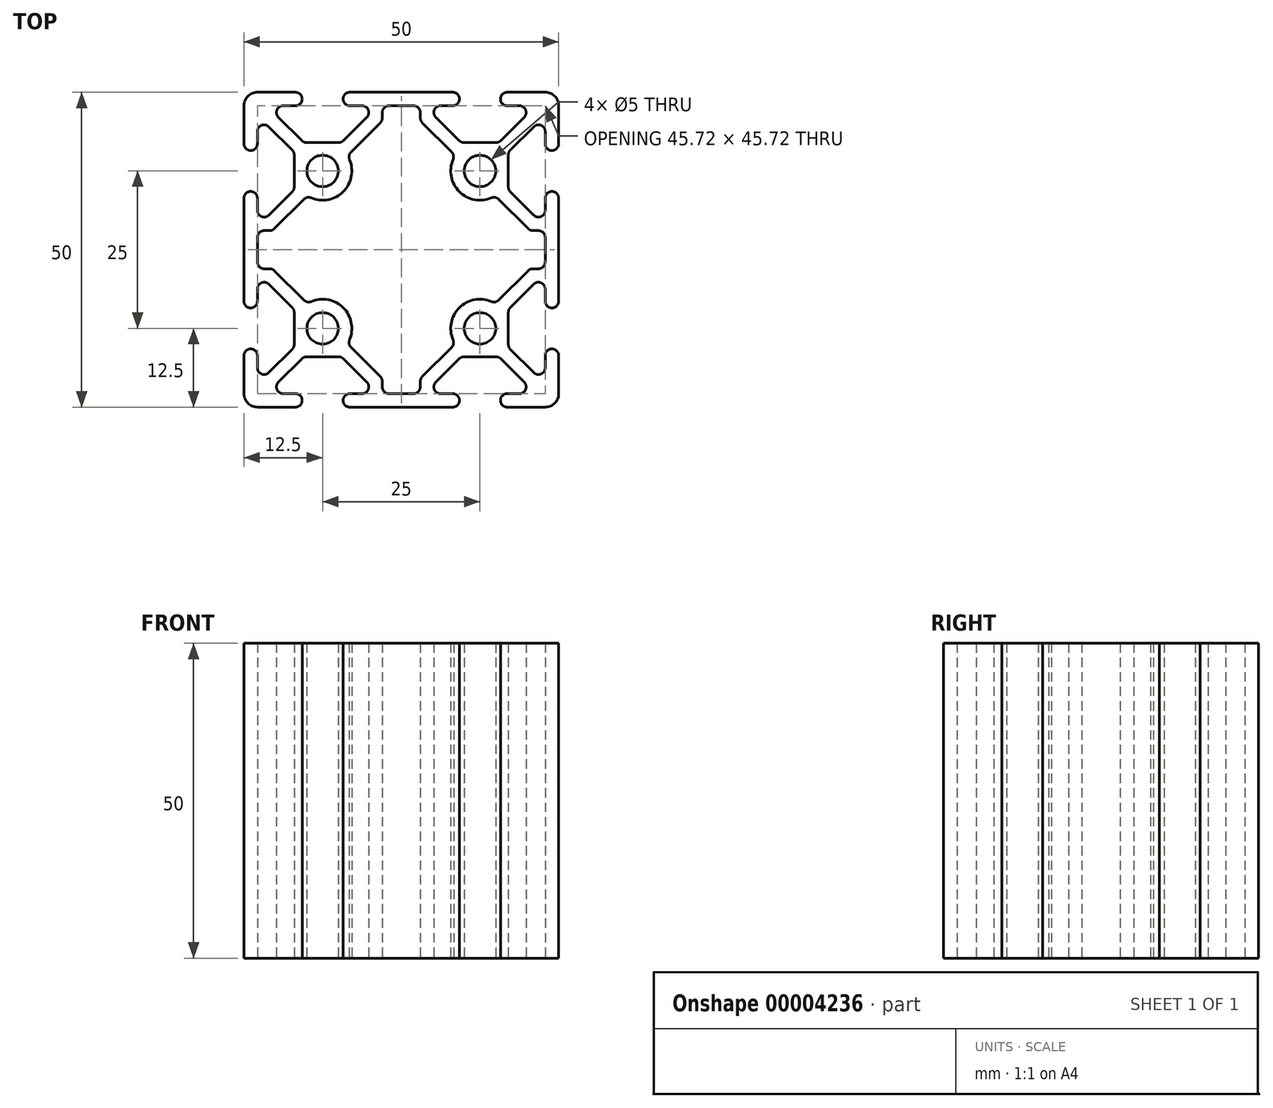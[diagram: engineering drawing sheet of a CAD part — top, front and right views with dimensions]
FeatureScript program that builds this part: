
annotation { "Feature Type Name" : "Feature", "Feature Type Description" : "" }
export const myFeature = defineFeature(function(context is Context, id is Id, definition is map)
    precondition{}
    {
        {
            var Q0;
            Q0=qCreatedBy(makeId("Top.planeOp"),FACE);
            var sketch = newSketch(context, id + "F0", { "sketchPlane" : qUnion([Q0])});
            skLineSegment(sketch, "E0", {"start": v(-12.5, 12.5) * mm, "end": v(-25, 25) * mm, "construction": true});
            skLineSegment(sketch, "E1", {"start": v(-25, 22.86) * mm, "end": v(-25, 16.82) * mm});
            skLineSegment(sketch, "E2", {"start": v(-22.86, 25) * mm, "end": v(-16.82, 25) * mm});
            skLineSegment(sketch, "E3", {"start": v(-16.82, 22.86) * mm, "end": v(-18.76, 22.86) * mm});
            skLineSegment(sketch, "E4", {"start": v(-22.86, 18.76) * mm, "end": v(-22.86, 16.82) * mm});
            skArc(sketch, "E5", {"start": v(-16.82, 25) * mm, "mid": v(-15.75, 23.93) * mm, "end": v(-16.82, 22.86) * mm});
            skArc(sketch, "E6", {"start": v(-22.86, 16.82) * mm, "mid": v(-23.93, 15.75) * mm, "end": v(-25, 16.82) * mm});
            skLineSegment(sketch, "E7", {"start": v(-19.52, 21.03) * mm, "end": v(-15.81, 17.32) * mm});
            skPoint(sketch, "E8.visualSharp", {"position": v(-25, 25) * mm});
            skLineSegment(sketch, "E8.filletArc", {"start": v(-25, 25) * mm, "end": v(-25, 25) * mm});
            skArc(sketch, "E9.filletArc", {"start": v(-21.03, 19.52) * mm, "mid": v(-22.2, 19.75) * mm, "end": v(-22.86, 18.76) * mm});
            skPoint(sketch, "E10.visualSharp", {"position": v(-21.35, 22.86) * mm});
            skArc(sketch, "E10.filletArc", {"start": v(-18.76, 22.86) * mm, "mid": v(-19.75, 22.2) * mm, "end": v(-19.52, 21.03) * mm});
            skArc(sketch, "E11.filletArc", {"start": v(-15.81, 17.32) * mm, "mid": v(-15.46, 17.1) * mm, "end": v(-15.05, 17.01) * mm});
            skCircle(sketch, "E12", {"center": v(-12.5, 12.5) * mm, "radius": 2.5 * mm});
            skLineSegment(sketch, "E13", {"start": v(0, 0) * mm, "end": v(0, 12.39) * mm, "construction": true});
            skCircle(sketch, "E14.0.MirrorC", {"center": v(12.5, 12.5) * mm, "radius": 2.5 * mm});
            skLineSegment(sketch, "E15", {"start": v(-12.5, 0) * mm, "end": v(-12.5, 12.5) * mm, "construction": true});
            skArc(sketch, "E16.0.MirrorCS", {"start": v(-9.19, 17.32) * mm, "mid": v(-9.54, 17.1) * mm, "end": v(-9.95, 17.01) * mm});
            skLineSegment(sketch, "E16.1.MirrorCS", {"start": v(-8.18, 22.86) * mm, "end": v(-6.24, 22.86) * mm});
            skLineSegment(sketch, "E16.3.MirrorCS", {"start": v(-5.48, 21.03) * mm, "end": v(-9.19, 17.32) * mm});
            skArc(sketch, "E16.8.MirrorCS", {"start": v(-8.18, 25) * mm, "mid": v(-9.25, 23.93) * mm, "end": v(-8.18, 22.86) * mm});
            skArc(sketch, "E16.11.MirrorCS", {"start": v(-6.24, 22.86) * mm, "mid": v(-5.25, 22.2) * mm, "end": v(-5.48, 21.03) * mm});
            skLineSegment(sketch, "E16.17.MirrorCS", {"start": v(0, 25) * mm, "end": v(-8.18, 25) * mm});
            skLineSegment(sketch, "E17", {"start": v(-15.05, 17.01) * mm, "end": v(-9.95, 17.01) * mm});
            skArc(sketch, "E18.1.MirrorCS", {"start": v(15.81, 17.32) * mm, "mid": v(15.46, 17.1) * mm, "end": v(15.05, 17.01) * mm});
            skArc(sketch, "E18.2.MirrorCS", {"start": v(9.19, 17.32) * mm, "mid": v(9.54, 17.1) * mm, "end": v(9.95, 17.01) * mm});
            skArc(sketch, "E18.3.MirrorCS", {"start": v(22.86, 16.82) * mm, "mid": v(23.93, 15.75) * mm, "end": v(25, 16.82) * mm});
            skLineSegment(sketch, "E18.5.MirrorCS", {"start": v(8.18, 22.86) * mm, "end": v(6.24, 22.86) * mm});
            skLineSegment(sketch, "E18.6.MirrorCS", {"start": v(19.52, 21.03) * mm, "end": v(15.81, 17.32) * mm});
            skLineSegment(sketch, "E18.7.MirrorCS", {"start": v(5.48, 21.03) * mm, "end": v(9.19, 17.32) * mm});
            skLineSegment(sketch, "E18.8.MirrorCS", {"start": v(12.5, 12.5) * mm, "end": v(25, 25) * mm, "construction": true});
            skArc(sketch, "E18.10.MirrorCS", {"start": v(16.82, 25) * mm, "mid": v(15.75, 23.93) * mm, "end": v(16.82, 22.86) * mm});
            skLineSegment(sketch, "E18.11.MirrorCS", {"start": v(15.05, 17.01) * mm, "end": v(9.95, 17.01) * mm});
            skPoint(sketch, "E18.12.MirrorP", {"position": v(21.35, 22.86) * mm});
            skLineSegment(sketch, "E18.14.MirrorCS", {"start": v(22.86, 25) * mm, "end": v(16.82, 25) * mm});
            skArc(sketch, "E18.15.MirrorCS", {"start": v(21.03, 19.52) * mm, "mid": v(22.2, 19.75) * mm, "end": v(22.86, 18.76) * mm});
            skPoint(sketch, "E18.16.MirrorP", {"position": v(25, 25) * mm});
            skLineSegment(sketch, "E18.17.MirrorCS", {"start": v(25, 22.86) * mm, "end": v(25, 16.82) * mm});
            skArc(sketch, "E18.18.MirrorCS", {"start": v(6.24, 22.86) * mm, "mid": v(5.25, 22.2) * mm, "end": v(5.48, 21.03) * mm});
            skArc(sketch, "E18.20.MirrorCS", {"start": v(18.76, 22.86) * mm, "mid": v(19.75, 22.2) * mm, "end": v(19.52, 21.03) * mm});
            skArc(sketch, "E18.21.MirrorCS", {"start": v(8.18, 25) * mm, "mid": v(9.25, 23.93) * mm, "end": v(8.18, 22.86) * mm});
            skLineSegment(sketch, "E18.22.MirrorCS", {"start": v(25, 25) * mm, "end": v(25, 25) * mm});
            skLineSegment(sketch, "E18.24.MirrorCS", {"start": v(22.86, 18.76) * mm, "end": v(22.86, 16.82) * mm});
            skLineSegment(sketch, "E18.25.MirrorCS", {"start": v(16.82, 22.86) * mm, "end": v(18.76, 22.86) * mm});
            skLineSegment(sketch, "E18.26.MirrorCS", {"start": v(0, 25) * mm, "end": v(8.18, 25) * mm});
            skLineSegment(sketch, "E19", {"start": v(-21.03, 19.52) * mm, "end": v(-17.32, 15.81) * mm});
            skLineSegment(sketch, "E20", {"start": v(0, 0) * mm, "end": v(-29.45, 0) * mm, "construction": true});
            skLineSegment(sketch, "E21", {"start": v(-17, 15.05) * mm, "end": v(-17, 12.5) * mm});
            skLineSegment(sketch, "E22", {"start": v(-12.5, 12.5) * mm, "end": v(-25, 12.5) * mm, "construction": true});
            skLineSegment(sketch, "E23.0.MirrorCS", {"start": v(21.03, 19.52) * mm, "end": v(17.32, 15.81) * mm});
            skLineSegment(sketch, "E24.0.MirrorCS", {"start": v(17, 15.05) * mm, "end": v(17, 12.5) * mm});
            skLineSegment(sketch, "E25.0.MirrorCS", {"start": v(-17, 9.95) * mm, "end": v(-17, 12.5) * mm});
            skLineSegment(sketch, "E26.0.MirrorCS", {"start": v(-21.03, 5.48) * mm, "end": v(-17.32, 9.19) * mm});
            skArc(sketch, "E27.0.MirrorCS", {"start": v(-21.03, 5.48) * mm, "mid": v(-22.2, 5.25) * mm, "end": v(-22.86, 6.24) * mm});
            skLineSegment(sketch, "E28.0.MirrorCS", {"start": v(-22.86, 6.24) * mm, "end": v(-22.86, 8.18) * mm});
            skArc(sketch, "E29.0.MirrorCS", {"start": v(-22.86, 8.18) * mm, "mid": v(-23.93, 9.25) * mm, "end": v(-25, 8.18) * mm});
            skLineSegment(sketch, "E30.0.MirrorCS", {"start": v(-25, 0) * mm, "end": v(-25, 8.18) * mm});
            skLineSegment(sketch, "E31.0.MirrorCS", {"start": v(17, 9.95) * mm, "end": v(17, 12.5) * mm});
            skLineSegment(sketch, "E32.0.MirrorCS", {"start": v(21.03, 5.48) * mm, "end": v(17.32, 9.19) * mm});
            skArc(sketch, "E33.0.MirrorCS", {"start": v(21.03, 5.48) * mm, "mid": v(22.2, 5.25) * mm, "end": v(22.86, 6.24) * mm});
            skLineSegment(sketch, "E34.0.MirrorCS", {"start": v(22.86, 6.24) * mm, "end": v(22.86, 8.18) * mm});
            skArc(sketch, "E35.0.MirrorCS", {"start": v(22.86, 8.18) * mm, "mid": v(23.93, 9.25) * mm, "end": v(25, 8.18) * mm});
            skLineSegment(sketch, "E36.0.MirrorCS", {"start": v(25, 0) * mm, "end": v(25, 8.18) * mm});
            skPoint(sketch, "E37.visualSharp", {"position": v(-17, 15.5) * mm});
            skArc(sketch, "E37.filletArc", {"start": v(-17, 15.05) * mm, "mid": v(-17.1, 15.46) * mm, "end": v(-17.32, 15.81) * mm});
            skPoint(sketch, "E38.visualSharp", {"position": v(-17, 9.5) * mm});
            skArc(sketch, "E38.filletArc", {"start": v(-17.32, 9.19) * mm, "mid": v(-17.1, 9.54) * mm, "end": v(-17, 9.95) * mm});
            skPoint(sketch, "E39.visualSharp", {"position": v(17, 9.5) * mm});
            skArc(sketch, "E39.filletArc", {"start": v(17, 9.95) * mm, "mid": v(17.1, 9.54) * mm, "end": v(17.32, 9.19) * mm});
            skPoint(sketch, "E40.visualSharp", {"position": v(17, 15.5) * mm});
            skArc(sketch, "E40.filletArc", {"start": v(17.32, 15.81) * mm, "mid": v(17.1, 15.46) * mm, "end": v(17, 15.05) * mm});
            skArc(sketch, "E41.0.MirrorCS", {"start": v(-17, -15.05) * mm, "mid": v(-17.1, -15.46) * mm, "end": v(-17.32, -15.81) * mm});
            skArc(sketch, "E41.1.MirrorCS", {"start": v(-17.32, -9.19) * mm, "mid": v(-17.1, -9.54) * mm, "end": v(-17, -9.95) * mm});
            skArc(sketch, "E41.2.MirrorCS", {"start": v(-9.19, -17.32) * mm, "mid": v(-9.54, -17.1) * mm, "end": v(-9.95, -17.01) * mm});
            skArc(sketch, "E41.3.MirrorCS", {"start": v(-15.81, -17.32) * mm, "mid": v(-15.46, -17.1) * mm, "end": v(-15.05, -17.01) * mm});
            skLineSegment(sketch, "E41.4.MirrorCS", {"start": v(-25, -25) * mm, "end": v(-25, -25) * mm});
            skLineSegment(sketch, "E41.5.MirrorCS", {"start": v(-22.86, -6.24) * mm, "end": v(-22.86, -8.18) * mm});
            skLineSegment(sketch, "E41.6.MirrorCS", {"start": v(-12.5, -12.5) * mm, "end": v(-25, -25) * mm, "construction": true});
            skLineSegment(sketch, "E41.7.MirrorCS", {"start": v(-8.18, -22.86) * mm, "end": v(-6.24, -22.86) * mm});
            skLineSegment(sketch, "E41.8.MirrorCS", {"start": v(-12.5, 0) * mm, "end": v(-12.5, -12.5) * mm, "construction": true});
            skLineSegment(sketch, "E41.9.MirrorCS", {"start": v(-5.48, -21.03) * mm, "end": v(-9.19, -17.32) * mm});
            skCircle(sketch, "E41.10.MirrorC", {"center": v(-12.5, -12.5) * mm, "radius": 2.5 * mm});
            skArc(sketch, "E41.11.MirrorCS", {"start": v(-18.76, -22.86) * mm, "mid": v(-19.75, -22.2) * mm, "end": v(-19.52, -21.03) * mm});
            skArc(sketch, "E41.12.MirrorCS", {"start": v(-21.03, -5.48) * mm, "mid": v(-22.2, -5.25) * mm, "end": v(-22.86, -6.24) * mm});
            skLineSegment(sketch, "E41.13.MirrorCS", {"start": v(-15.05, -17.01) * mm, "end": v(-9.95, -17.01) * mm});
            skPoint(sketch, "E41.14.MirrorP", {"position": v(-17, -9.5) * mm});
            skLineSegment(sketch, "E41.15.MirrorCS", {"start": v(-21.03, -5.48) * mm, "end": v(-17.32, -9.19) * mm});
            skLineSegment(sketch, "E41.16.MirrorCS", {"start": v(-19.52, -21.03) * mm, "end": v(-15.81, -17.32) * mm});
            skArc(sketch, "E41.17.MirrorCS", {"start": v(-6.24, -22.86) * mm, "mid": v(-5.25, -22.2) * mm, "end": v(-5.48, -21.03) * mm});
            skLineSegment(sketch, "E41.18.MirrorCS", {"start": v(-25, 0) * mm, "end": v(-25, -8.18) * mm});
            skArc(sketch, "E41.19.MirrorCS", {"start": v(-21.03, -19.52) * mm, "mid": v(-22.2, -19.75) * mm, "end": v(-22.86, -18.76) * mm});
            skArc(sketch, "E41.20.MirrorCS", {"start": v(-16.82, -25) * mm, "mid": v(-15.75, -23.93) * mm, "end": v(-16.82, -22.86) * mm});
            skArc(sketch, "E41.21.MirrorCS", {"start": v(-22.86, -16.82) * mm, "mid": v(-23.93, -15.75) * mm, "end": v(-25, -16.82) * mm});
            skLineSegment(sketch, "E41.22.MirrorCS", {"start": v(-17, -15.05) * mm, "end": v(-17, -12.5) * mm});
            skPoint(sketch, "E41.23.MirrorP", {"position": v(-17, -15.5) * mm});
            skArc(sketch, "E41.24.MirrorCS", {"start": v(-22.86, -8.18) * mm, "mid": v(-23.93, -9.25) * mm, "end": v(-25, -8.18) * mm});
            skLineSegment(sketch, "E41.25.MirrorCS", {"start": v(-21.03, -19.52) * mm, "end": v(-17.32, -15.81) * mm});
            skPoint(sketch, "E41.26.MirrorP", {"position": v(-21.35, -22.86) * mm});
            skArc(sketch, "E41.27.MirrorCS", {"start": v(-8.18, -25) * mm, "mid": v(-9.25, -23.93) * mm, "end": v(-8.18, -22.86) * mm});
            skPoint(sketch, "E41.28.MirrorP", {"position": v(-25, -25) * mm});
            skLineSegment(sketch, "E41.29.MirrorCS", {"start": v(-12.5, -12.5) * mm, "end": v(-25, -12.5) * mm, "construction": true});
            skLineSegment(sketch, "E41.30.MirrorCS", {"start": v(-17, -9.95) * mm, "end": v(-17, -12.5) * mm});
            skLineSegment(sketch, "E41.31.MirrorCS", {"start": v(-16.82, -22.86) * mm, "end": v(-18.76, -22.86) * mm});
            skLineSegment(sketch, "E41.32.MirrorCS", {"start": v(-22.86, -18.76) * mm, "end": v(-22.86, -16.82) * mm});
            skLineSegment(sketch, "E41.33.MirrorCS", {"start": v(-25, -22.86) * mm, "end": v(-25, -16.82) * mm});
            skLineSegment(sketch, "E41.34.MirrorCS", {"start": v(-22.86, -25) * mm, "end": v(-16.82, -25) * mm});
            skLineSegment(sketch, "E41.35.MirrorCS", {"start": v(0, -25) * mm, "end": v(-8.18, -25) * mm});
            skArc(sketch, "E42.0.MirrorCS", {"start": v(17.32, -15.81) * mm, "mid": v(17.1, -15.46) * mm, "end": v(17, -15.05) * mm});
            skArc(sketch, "E42.1.MirrorCS", {"start": v(17, -9.95) * mm, "mid": v(17.1, -9.54) * mm, "end": v(17.32, -9.19) * mm});
            skArc(sketch, "E42.2.MirrorCS", {"start": v(9.19, -17.32) * mm, "mid": v(9.54, -17.1) * mm, "end": v(9.95, -17.01) * mm});
            skLineSegment(sketch, "E42.3.MirrorCS", {"start": v(22.86, -6.24) * mm, "end": v(22.86, -8.18) * mm});
            skLineSegment(sketch, "E42.4.MirrorCS", {"start": v(16.82, -22.86) * mm, "end": v(18.76, -22.86) * mm});
            skArc(sketch, "E42.5.MirrorCS", {"start": v(15.81, -17.32) * mm, "mid": v(15.46, -17.1) * mm, "end": v(15.05, -17.01) * mm});
            skLineSegment(sketch, "E42.6.MirrorCS", {"start": v(25, -25) * mm, "end": v(25, -25) * mm});
            skArc(sketch, "E42.7.MirrorCS", {"start": v(22.86, -16.82) * mm, "mid": v(23.93, -15.75) * mm, "end": v(25, -16.82) * mm});
            skArc(sketch, "E42.8.MirrorCS", {"start": v(16.82, -25) * mm, "mid": v(15.75, -23.93) * mm, "end": v(16.82, -22.86) * mm});
            skPoint(sketch, "E42.9.MirrorP", {"position": v(25, -25) * mm});
            skArc(sketch, "E42.10.MirrorCS", {"start": v(21.03, -5.48) * mm, "mid": v(22.2, -5.25) * mm, "end": v(22.86, -6.24) * mm});
            skLineSegment(sketch, "E42.11.MirrorCS", {"start": v(0, -25) * mm, "end": v(8.18, -25) * mm});
            skArc(sketch, "E42.12.MirrorCS", {"start": v(8.18, -25) * mm, "mid": v(9.25, -23.93) * mm, "end": v(8.18, -22.86) * mm});
            skLineSegment(sketch, "E42.13.MirrorCS", {"start": v(22.86, -25) * mm, "end": v(16.82, -25) * mm});
            skPoint(sketch, "E42.14.MirrorP", {"position": v(17, -15.5) * mm});
            skArc(sketch, "E42.15.MirrorCS", {"start": v(21.03, -19.52) * mm, "mid": v(22.2, -19.75) * mm, "end": v(22.86, -18.76) * mm});
            skLineSegment(sketch, "E42.16.MirrorCS", {"start": v(17, -9.95) * mm, "end": v(17, -12.5) * mm});
            skLineSegment(sketch, "E42.17.MirrorCS", {"start": v(22.86, -18.76) * mm, "end": v(22.86, -16.82) * mm});
            skArc(sketch, "E42.18.MirrorCS", {"start": v(6.24, -22.86) * mm, "mid": v(5.25, -22.2) * mm, "end": v(5.48, -21.03) * mm});
            skLineSegment(sketch, "E42.19.MirrorCS", {"start": v(5.48, -21.03) * mm, "end": v(9.19, -17.32) * mm});
            skLineSegment(sketch, "E42.20.MirrorCS", {"start": v(15.05, -17.01) * mm, "end": v(9.95, -17.01) * mm});
            skLineSegment(sketch, "E42.21.MirrorCS", {"start": v(17, -15.05) * mm, "end": v(17, -12.5) * mm});
            skArc(sketch, "E42.22.MirrorCS", {"start": v(22.86, -8.18) * mm, "mid": v(23.93, -9.25) * mm, "end": v(25, -8.18) * mm});
            skLineSegment(sketch, "E42.23.MirrorCS", {"start": v(8.18, -22.86) * mm, "end": v(6.24, -22.86) * mm});
            skPoint(sketch, "E42.24.MirrorP", {"position": v(17, -9.5) * mm});
            skLineSegment(sketch, "E42.25.MirrorCS", {"start": v(21.03, -5.48) * mm, "end": v(17.32, -9.19) * mm});
            skLineSegment(sketch, "E42.26.MirrorCS", {"start": v(25, -22.86) * mm, "end": v(25, -16.82) * mm});
            skCircle(sketch, "E42.27.MirrorC", {"center": v(12.5, -12.5) * mm, "radius": 2.5 * mm});
            skLineSegment(sketch, "E42.28.MirrorCS", {"start": v(12.5, -12.5) * mm, "end": v(25, -25) * mm, "construction": true});
            skPoint(sketch, "E42.29.MirrorP", {"position": v(21.35, -22.86) * mm});
            skLineSegment(sketch, "E42.30.MirrorCS", {"start": v(25, 0) * mm, "end": v(25, -8.18) * mm});
            skArc(sketch, "E42.31.MirrorCS", {"start": v(22.86, -16.82) * mm, "mid": v(23.93, -15.75) * mm, "end": v(25, -16.82) * mm});
            skLineSegment(sketch, "E42.32.MirrorCS", {"start": v(19.52, -21.03) * mm, "end": v(15.81, -17.32) * mm});
            skLineSegment(sketch, "E42.33.MirrorCS", {"start": v(21.03, -19.52) * mm, "end": v(17.32, -15.81) * mm});
            skArc(sketch, "E42.34.MirrorCS", {"start": v(18.76, -22.86) * mm, "mid": v(19.75, -22.2) * mm, "end": v(19.52, -21.03) * mm});
            skArc(sketch, "E43.filletArc", {"start": v(-22.86, 25) * mm, "mid": v(-24.37, 24.37) * mm, "end": v(-25, 22.86) * mm});
            skArc(sketch, "E44.filletArc", {"start": v(25, 22.86) * mm, "mid": v(24.37, 24.37) * mm, "end": v(22.86, 25) * mm});
            skArc(sketch, "E45.filletArc", {"start": v(22.86, -25) * mm, "mid": v(24.37, -24.37) * mm, "end": v(25, -22.86) * mm});
            skArc(sketch, "E46.filletArc", {"start": v(-25, -22.86) * mm, "mid": v(-24.37, -24.37) * mm, "end": v(-22.86, -25) * mm});
            skLineSegment(sketch, "E47", {"start": v(0, 22.86) * mm, "end": v(1.96, 22.86) * mm});
            skLineSegment(sketch, "E48", {"start": v(3.03, 21.8) * mm, "end": v(3.03, 20.9) * mm});
            skArc(sketch, "E49.0", {"start": v(14.31, 8.23) * mm, "mid": v(9.22, 9.22) * mm, "end": v(8.23, 14.31) * mm});
            skLineSegment(sketch, "E50.0", {"start": v(3.34, 20.15) * mm, "end": v(8, 15.49) * mm});
            skPoint(sketch, "E51.visualSharp", {"position": v(3.03, 22.86) * mm});
            skArc(sketch, "E51.filletArc", {"start": v(3.03, 21.8) * mm, "mid": v(2.71, 22.55) * mm, "end": v(1.96, 22.86) * mm});
            skPoint(sketch, "E52.visualSharp", {"position": v(8.55, 14.94) * mm});
            skArc(sketch, "E52.filletArc", {"start": v(8.23, 14.31) * mm, "mid": v(8.3, 14.93) * mm, "end": v(8, 15.49) * mm});
            skArc(sketch, "E53.0.MirrorCS", {"start": v(-14.31, 8.23) * mm, "mid": v(-9.22, 9.22) * mm, "end": v(-8.23, 14.31) * mm});
            skArc(sketch, "E54.0.MirrorCS", {"start": v(-8.23, 14.31) * mm, "mid": v(-8.3, 14.93) * mm, "end": v(-8, 15.49) * mm});
            skArc(sketch, "E55.0.MirrorCS", {"start": v(-3.03, 21.8) * mm, "mid": v(-2.71, 22.55) * mm, "end": v(-1.96, 22.86) * mm});
            skLineSegment(sketch, "E56.0.MirrorCS", {"start": v(0, 22.86) * mm, "end": v(-1.96, 22.86) * mm});
            skPoint(sketch, "E57.visualSharp", {"position": v(3.03, 20.46) * mm});
            skArc(sketch, "E57.filletArc", {"start": v(3.03, 20.9) * mm, "mid": v(3.1, 20.5) * mm, "end": v(3.34, 20.15) * mm});
            skLineSegment(sketch, "E58.0.MirrorCS", {"start": v(-3.34, 20.15) * mm, "end": v(-8, 15.49) * mm});
            skArc(sketch, "E59.0.MirrorCS", {"start": v(-3.03, 20.9) * mm, "mid": v(-3.1, 20.5) * mm, "end": v(-3.34, 20.15) * mm});
            skLineSegment(sketch, "E60.0.MirrorCS", {"start": v(-3.03, 21.8) * mm, "end": v(-3.03, 20.9) * mm});
            skPoint(sketch, "E61.visualSharp", {"position": v(-12.5, 7.86) * mm});
            skPoint(sketch, "E62.visualSharp", {"position": v(-12.5, -7.86) * mm});
            skPoint(sketch, "E63.visualSharp", {"position": v(12.5, -7.86) * mm});
            skArc(sketch, "E64.0.MirrorCS", {"start": v(-14.31, 8.23) * mm, "mid": v(-14.93, 8.3) * mm, "end": v(-15.49, 8) * mm});
            skLineSegment(sketch, "E65.0.MirrorCS", {"start": v(-20.15, 3.34) * mm, "end": v(-15.49, 8) * mm});
            skArc(sketch, "E66.0.MirrorCS", {"start": v(-20.9, 3.03) * mm, "mid": v(-20.5, 3.1) * mm, "end": v(-20.15, 3.34) * mm});
            skLineSegment(sketch, "E67.0.MirrorCS", {"start": v(-21.79, 3.03) * mm, "end": v(-20.9, 3.03) * mm});
            skArc(sketch, "E68.0.MirrorCS", {"start": v(-21.79, 3.03) * mm, "mid": v(-22.55, 2.71) * mm, "end": v(-22.86, 1.96) * mm});
            skLineSegment(sketch, "E69.0.MirrorCS", {"start": v(-22.86, 0) * mm, "end": v(-22.86, 1.96) * mm});
            skArc(sketch, "E70.0.MirrorCS", {"start": v(14.31, 8.23) * mm, "mid": v(14.93, 8.3) * mm, "end": v(15.49, 8) * mm});
            skArc(sketch, "E71.0.MirrorCS", {"start": v(-12.5, 7.86) * mm, "mid": v(-8.63, 9.94) * mm, "end": v(-8.23, 14.31) * mm});
            skLineSegment(sketch, "E72.0.MirrorCS", {"start": v(20.15, 3.34) * mm, "end": v(15.49, 8) * mm});
            skArc(sketch, "E73.0.MirrorCS", {"start": v(20.9, 3.03) * mm, "mid": v(20.5, 3.1) * mm, "end": v(20.15, 3.34) * mm});
            skLineSegment(sketch, "E74.0.MirrorCS", {"start": v(21.79, 3.03) * mm, "end": v(20.9, 3.03) * mm});
            skArc(sketch, "E75.0.MirrorCS", {"start": v(21.79, 3.03) * mm, "mid": v(22.55, 2.71) * mm, "end": v(22.86, 1.96) * mm});
            skLineSegment(sketch, "E76.0.MirrorCS", {"start": v(22.86, 0) * mm, "end": v(22.86, 1.96) * mm});
            skPoint(sketch, "E77.orphan", {"position": v(12.5, 7.86) * mm});
            skArc(sketch, "E78.0.MirrorCS", {"start": v(-20.9, -3.03) * mm, "mid": v(-20.5, -3.1) * mm, "end": v(-20.15, -3.34) * mm});
            skLineSegment(sketch, "E78.1.MirrorCS", {"start": v(-21.79, -3.03) * mm, "end": v(-20.9, -3.03) * mm});
            skArc(sketch, "E78.2.MirrorCS", {"start": v(-21.79, -3.03) * mm, "mid": v(-22.55, -2.71) * mm, "end": v(-22.86, -1.96) * mm});
            skLineSegment(sketch, "E78.3.MirrorCS", {"start": v(-22.86, 0) * mm, "end": v(-22.86, -1.96) * mm});
            skLineSegment(sketch, "E79.0.MirrorCS", {"start": v(-20.15, -3.34) * mm, "end": v(-15.49, -8) * mm});
            skArc(sketch, "E80.0.MirrorCS", {"start": v(-14.31, -8.23) * mm, "mid": v(-14.93, -8.3) * mm, "end": v(-15.49, -8) * mm});
            skArc(sketch, "E81.0.MirrorCS", {"start": v(-14.31, -8.23) * mm, "mid": v(-9.22, -9.22) * mm, "end": v(-8.23, -14.31) * mm});
            skArc(sketch, "E82.0.MirrorCS", {"start": v(-8.23, -14.31) * mm, "mid": v(-8.3, -14.93) * mm, "end": v(-8, -15.49) * mm});
            skLineSegment(sketch, "E83.0.MirrorCS", {"start": v(-3.34, -20.15) * mm, "end": v(-8, -15.49) * mm});
            skArc(sketch, "E84.0.MirrorCS", {"start": v(-3.03, -20.9) * mm, "mid": v(-3.1, -20.5) * mm, "end": v(-3.34, -20.15) * mm});
            skLineSegment(sketch, "E85.0.MirrorCS", {"start": v(-3.03, -21.8) * mm, "end": v(-3.03, -20.9) * mm});
            skArc(sketch, "E86.0.MirrorCS", {"start": v(-3.03, -21.8) * mm, "mid": v(-2.71, -22.55) * mm, "end": v(-1.96, -22.86) * mm});
            skLineSegment(sketch, "E87.0.MirrorCS", {"start": v(0, -22.86) * mm, "end": v(-1.96, -22.86) * mm});
            skLineSegment(sketch, "E88.0.MirrorCS", {"start": v(0, -22.86) * mm, "end": v(1.96, -22.86) * mm});
            skArc(sketch, "E89.0.MirrorCS", {"start": v(3.03, -21.8) * mm, "mid": v(2.71, -22.55) * mm, "end": v(1.96, -22.86) * mm});
            skLineSegment(sketch, "E90.0.MirrorCS", {"start": v(3.03, -21.8) * mm, "end": v(3.03, -20.9) * mm});
            skArc(sketch, "E91.0.MirrorCS", {"start": v(3.03, -20.9) * mm, "mid": v(3.1, -20.5) * mm, "end": v(3.34, -20.15) * mm});
            skLineSegment(sketch, "E92.0.MirrorCS", {"start": v(3.34, -20.15) * mm, "end": v(8, -15.49) * mm});
            skArc(sketch, "E93.0.MirrorCS", {"start": v(8.23, -14.31) * mm, "mid": v(8.3, -14.93) * mm, "end": v(8, -15.49) * mm});
            skArc(sketch, "E94.0.MirrorCS", {"start": v(14.31, -8.23) * mm, "mid": v(9.22, -9.22) * mm, "end": v(8.23, -14.31) * mm});
            skArc(sketch, "E95.0.MirrorCS", {"start": v(14.31, -8.23) * mm, "mid": v(14.93, -8.3) * mm, "end": v(15.49, -8) * mm});
            skLineSegment(sketch, "E96.0.MirrorCS", {"start": v(20.15, -3.34) * mm, "end": v(15.49, -8) * mm});
            skArc(sketch, "E97.0.MirrorCS", {"start": v(20.9, -3.03) * mm, "mid": v(20.5, -3.1) * mm, "end": v(20.15, -3.34) * mm});
            skLineSegment(sketch, "E98.0.MirrorCS", {"start": v(21.79, -3.03) * mm, "end": v(20.9, -3.03) * mm});
            skArc(sketch, "E99.0.MirrorCS", {"start": v(21.79, -3.03) * mm, "mid": v(22.55, -2.71) * mm, "end": v(22.86, -1.96) * mm});
            skLineSegment(sketch, "E100.0.MirrorCS", {"start": v(22.86, 0) * mm, "end": v(22.86, -1.96) * mm});
            skSolve(sketch);
        }
        {
            var Q0;
            Q0=makeQuery(id+"F0.imprint","IMPRINT",FACE,{"disambiguationData":[TD([[makeQuery(id+"F0.imprint","IMPRINT",EDGE,{"derivedFrom":sQuery(id+"F0.wireOp",EDGE,"E1")}),1.0]])]});
            extrude(context, id + "F1", {"entities" : qUnion([Q0]), "depth" : 50 * mm});
        }
    });
